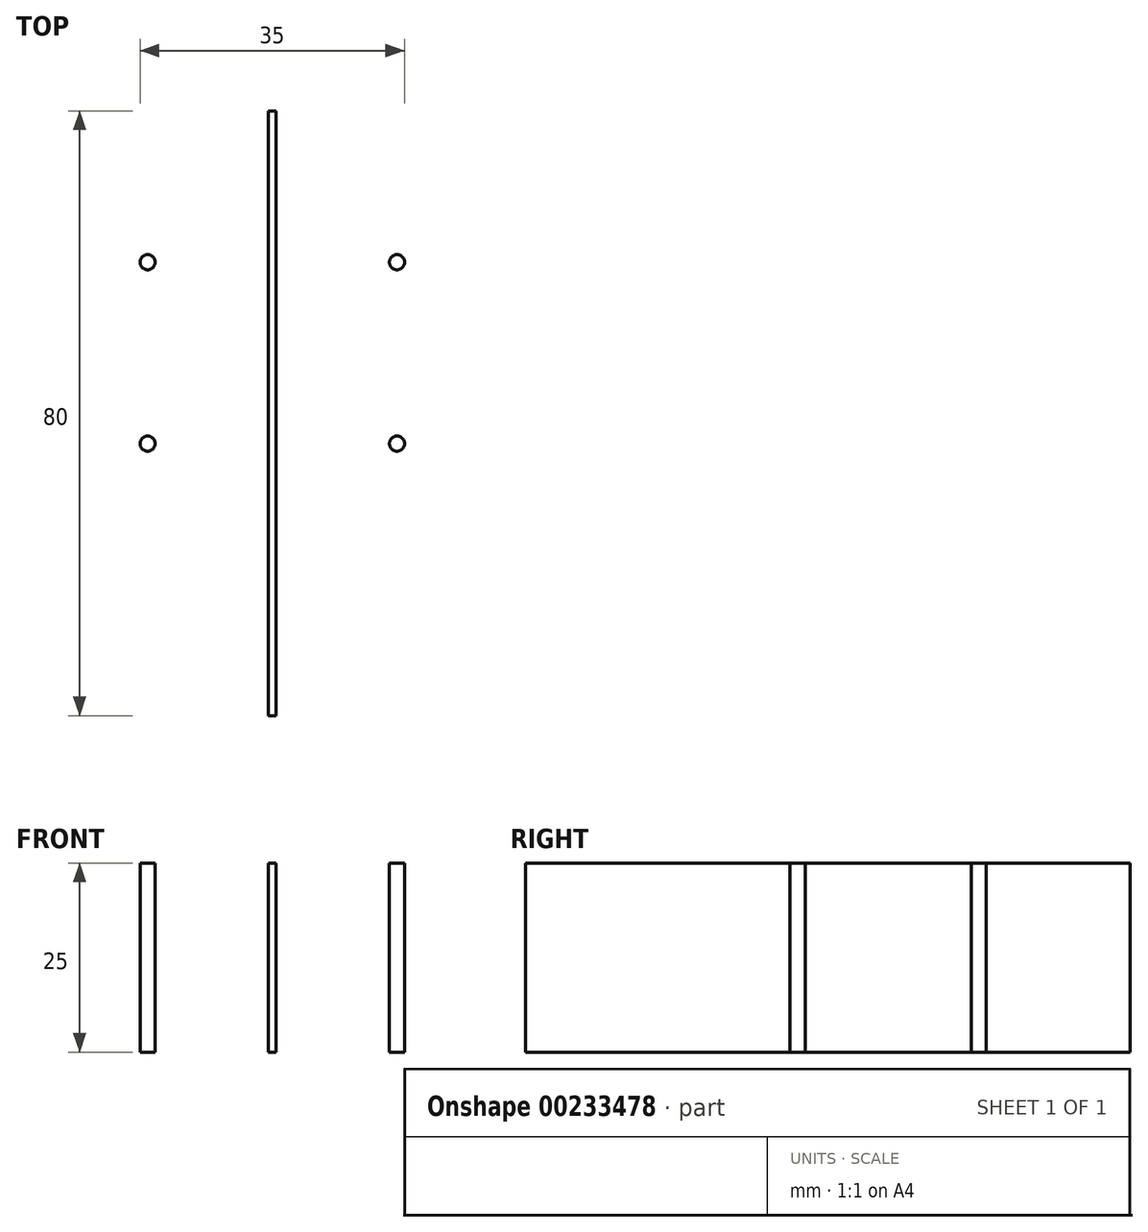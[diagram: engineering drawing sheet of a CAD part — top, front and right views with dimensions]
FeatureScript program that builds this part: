
annotation { "Feature Type Name" : "Feature", "Feature Type Description" : "" }
export const myFeature = defineFeature(function(context is Context, id is Id, definition is map)
    precondition{}
    {
        {
            var Q0;
            Q0=qCreatedBy(makeId("Top.planeOp"),FACE);
            var sketch = newSketch(context, id + "F0", { "sketchPlane" : qUnion([Q0])});
            skLineSegment(sketch, "E0.top", {"start": v(-3.42, 80) * mm, "end": v(-73.42, 80) * mm});
            skLineSegment(sketch, "E1.bottom", {"start": v(-21.19, 80) * mm, "end": v(-20.19, 80) * mm});
            skLineSegment(sketch, "E1.top", {"start": v(-21.19, 0) * mm, "end": v(-20.19, 0) * mm});
            skLineSegment(sketch, "E1.left", {"start": v(-21.19, 80) * mm, "end": v(-21.19, 0) * mm});
            skLineSegment(sketch, "E1.right", {"start": v(-20.19, 80) * mm, "end": v(-20.19, 0) * mm});
            skLineSegment(sketch, "E2", {"start": v(-20.69, 80) * mm, "end": v(-20.69, 0) * mm});
            skPoint(sketch, "E3", {"position": v(-37.19, 60) * mm});
            skPoint(sketch, "E4", {"position": v(-37.19, 36) * mm});
            skCircle(sketch, "E5", {"center": v(-37.19, 60) * mm, "radius": 1 * mm});
            skCircle(sketch, "E6", {"center": v(-37.19, 36) * mm, "radius": 1 * mm});
            skCircle(sketch, "E7.MirrorC", {"center": v(-4.19, 60) * mm, "radius": 1 * mm});
            skCircle(sketch, "E8.MirrorC", {"center": v(-4.19, 36) * mm, "radius": 1 * mm});
            skSolve(sketch);
        }
        {
            var Q0;
            Q0=qSketchRegion(id+"F0",true);
            extrude(context, id + "F1", {"entities" : qUnion([Q0]), "depth" : 25 * mm, "offsetDistance" : 25 * mm});
        }
    });
